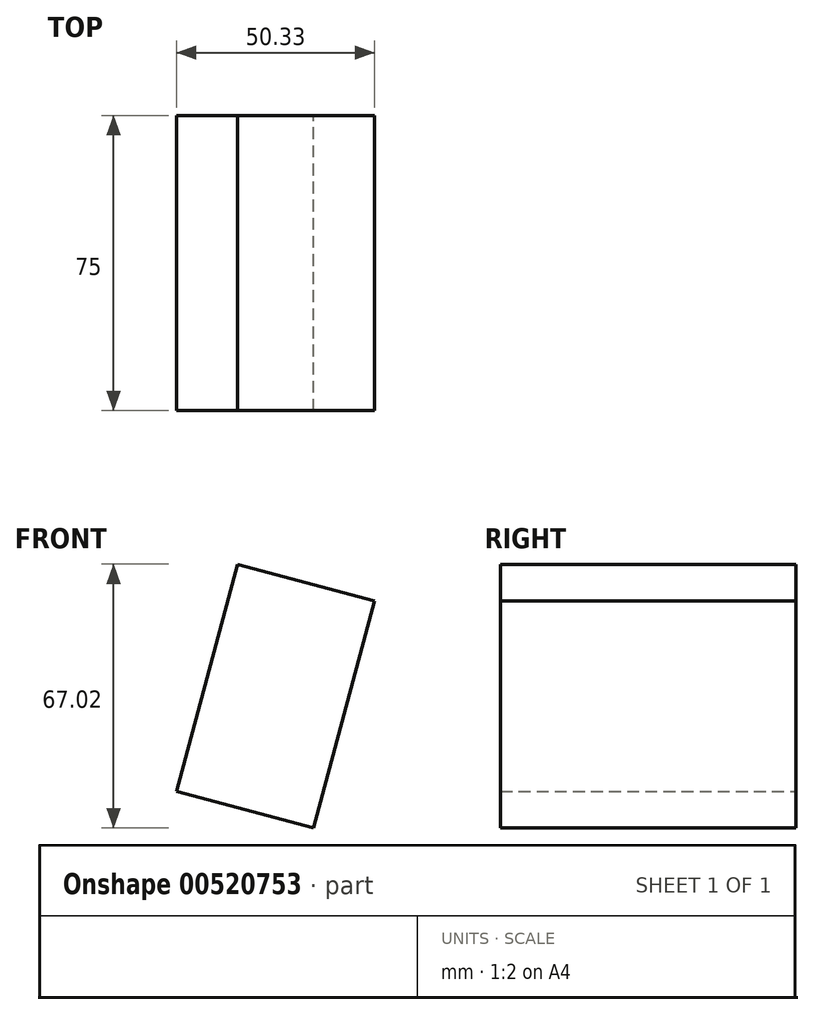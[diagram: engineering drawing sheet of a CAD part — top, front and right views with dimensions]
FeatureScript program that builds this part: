
annotation { "Feature Type Name" : "Feature", "Feature Type Description" : "" }
export const myFeature = defineFeature(function(context is Context, id is Id, definition is map)
    precondition{}
    {
        {
            var Q0;
            Q0=qCreatedBy(makeId("Front.planeOp"),FACE);
            var sketch = newSketch(context, id + "F0", { "sketchPlane" : qUnion([Q0])});
            skLineSegment(sketch, "E0.bottom", {"start": v(-1.23, -9.34) * mm, "end": v(-36.1, 0) * mm});
            skLineSegment(sketch, "E0.top", {"start": v(14.23, 48.34) * mm, "end": v(-20.64, 57.68) * mm});
            skLineSegment(sketch, "E0.left", {"start": v(-1.23, -9.34) * mm, "end": v(14.23, 48.34) * mm});
            skLineSegment(sketch, "E0.right", {"start": v(-36.1, 0) * mm, "end": v(-20.64, 57.68) * mm});
            skSolve(sketch);
        }
        {
            var Q0;
            Q0=makeQuery(id+"F0.imprint","IMPRINT",FACE,{"disambiguationData":[TD([[makeQuery(id+"F0.imprint","IMPRINT",EDGE,{"derivedFrom":sQuery(id+"F0.wireOp",EDGE,"E0.bottom")}),-1.0]])]});
            extrude(context, id + "F1", {"entities" : qUnion([Q0]), "depth" : 75 * mm, "offsetDistance" : 25 * mm});
        }
    });
